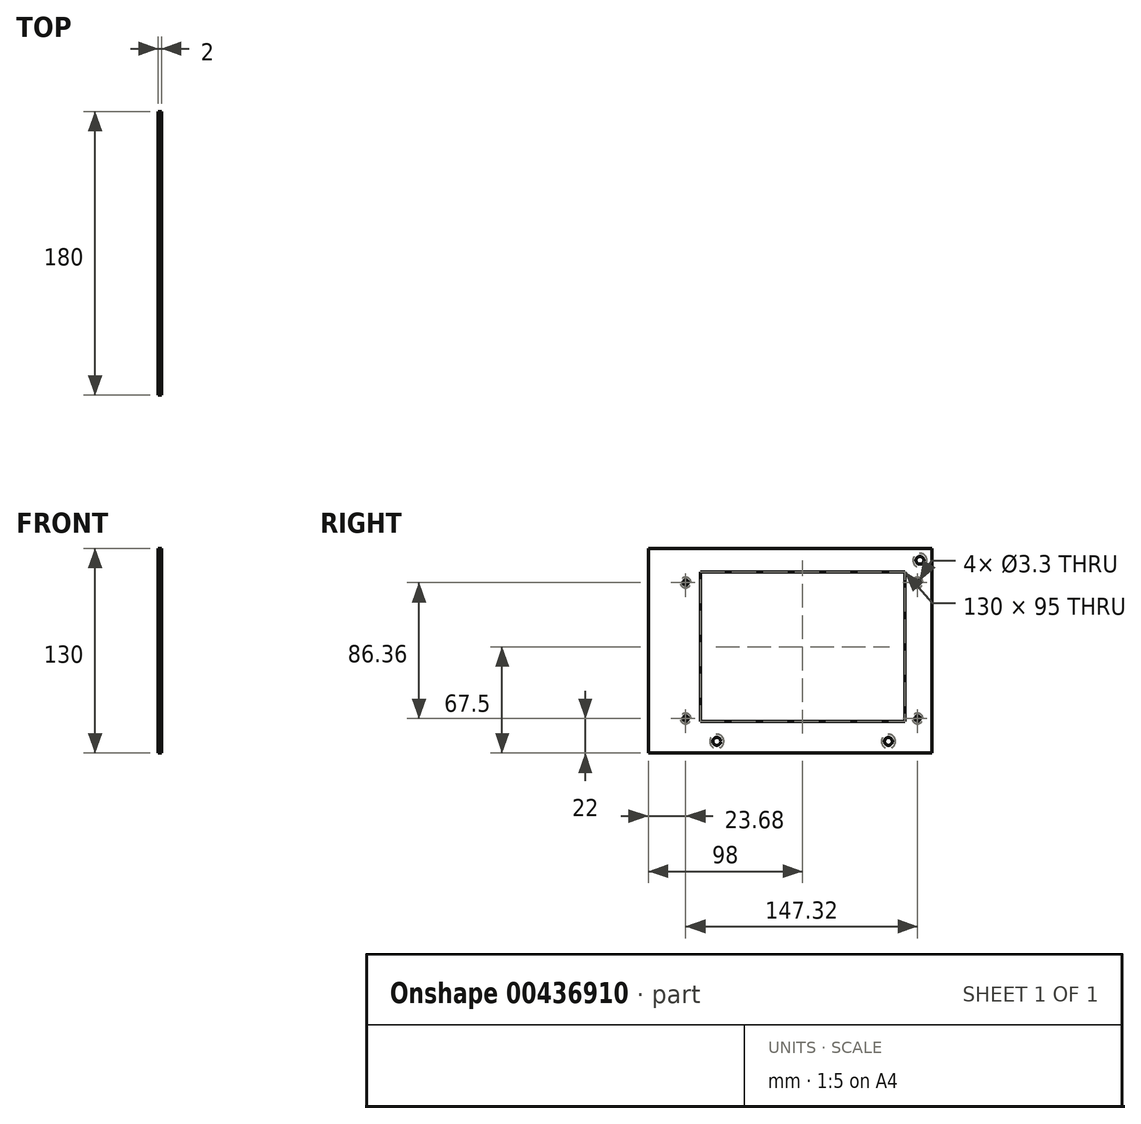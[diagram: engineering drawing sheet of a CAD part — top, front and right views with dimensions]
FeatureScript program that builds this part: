
annotation { "Feature Type Name" : "Feature", "Feature Type Description" : "" }
export const myFeature = defineFeature(function(context is Context, id is Id, definition is map)
    precondition{}
    {
        {
            var Q0;
            Q0=qCreatedBy(makeId("Right.planeOp"),FACE);
            var sketch = newSketch(context, id + "F0", { "sketchPlane" : qUnion([Q0])});
            skLineSegment(sketch, "E0.bottom", {"start": v(0, 0) * mm, "end": v(180, 0) * mm});
            skLineSegment(sketch, "E0.top", {"start": v(0, 130) * mm, "end": v(180, 130) * mm});
            skLineSegment(sketch, "E0.left", {"start": v(0, 0) * mm, "end": v(0, 130) * mm});
            skLineSegment(sketch, "E0.right", {"start": v(180, 0) * mm, "end": v(180, 130) * mm});
            skSolve(sketch);
        }
        {
            var Q0;
            Q0 = qSketchRegion(id + "F0", true);
            extrude(context, id + "F1", {"entities" : qUnion([Q0]), "depth" : 2 * mm});
        }
        {
            var Q0;
            Q0=makeQuery(id+"F1.opExtrude","CAP_FACE",FACE,{"disambiguationData":[OSD([sQuery(id+"F0.wireOp",EDGE,"E0.bottom"),sQuery(id+"F0.wireOp",EDGE,"E0.top"),sQuery(id+"F0.wireOp",EDGE,"E0.left"),sQuery(id+"F0.wireOp",EDGE,"E0.right")])],"isStart":true});
            var sketch = newSketch(context, id + "F2", { "sketchPlane" : qUnion([Q0])});
            skPoint(sketch, "E1", {"position": v(-171, 22) * mm});
            skPoint(sketch, "E2.0.1.0", {"position": v(-171, 108.36) * mm});
            skPoint(sketch, "E2.1.0.0", {"position": v(-23.68, 22) * mm});
            skPoint(sketch, "E2.1.1.0", {"position": v(-23.68, 108.36) * mm});
            skLineSegment(sketch, "E2.direction1", {"start": v(-171, 22) * mm, "end": v(-23.68, 22) * mm, "construction": true});
            skLineSegment(sketch, "E2.direction2", {"start": v(-171, 22) * mm, "end": v(-171, 108.36) * mm, "construction": true});
            skSolve(sketch);
        }
        {
            var Q0;
            Q0=sQuery(id+"F2.wireOp",VERTEX,"E2.0.1.0");
            var Q1;
            Q1=sQuery(id+"F2.wireOp",VERTEX,"E1");
            var Q2;
            Q2=sQuery(id+"F2.wireOp",VERTEX,"E2.1.0.0");
            var Q3;
            Q3=sQuery(id+"F2.wireOp",VERTEX,"E2.1.1.0");
            var Q4;
            Q4=makeQuery(id+"F1.opExtrude","SWEPT_BODY",BODY,{"disambiguationData":[OSD([sQuery(id+"F0.wireOp",EDGE,"E0.bottom"),sQuery(id+"F0.wireOp",EDGE,"E0.top"),sQuery(id+"F0.wireOp",EDGE,"E0.left"),sQuery(id+"F0.wireOp",EDGE,"E0.right")])]});
            hole(context, id + "F3", {"style" : HoleStyle.C_SINK, "endStyle" : HoleEndStyle.THROUGH, "standardTappedOrClearance" : lookupTablePath({ "standard" : "ISO", "fit" : "Normal", "size" : "M3", "type" : "Clearance" }), "standardBlindInLast" : lookupTablePath({ "fit" : "Standard", "standard" : "ISO", "size" : "M3", "type" : "Clearance" }), "holeDiameter" : 3.3 * mm, "cSinkDiameter" : 6.72 * mm, "cSinkAngle" : 90 * degree, "isTappedThrough" : true, "tappedDepth" : 12 * mm, "tapClearance" : 3, "locations" : qUnion([Q0, Q1, Q2, Q3]), "scope" : qUnion([Q4])});
        }
        {
            var Q0;
            Q0=makeQuery(id+"F1.opExtrude","CAP_FACE",FACE,{"disambiguationData":[OSD([sQuery(id+"F0.wireOp",EDGE,"E0.bottom"),sQuery(id+"F0.wireOp",EDGE,"E0.top"),sQuery(id+"F0.wireOp",EDGE,"E0.left"),sQuery(id+"F0.wireOp",EDGE,"E0.right")])],"isStart":true});
            var sketch = newSketch(context, id + "F4", { "sketchPlane" : qUnion([Q0])});
            skLineSegment(sketch, "E3.bottom", {"start": v(-163, 20) * mm, "end": v(-33, 20) * mm});
            skLineSegment(sketch, "E3.top", {"start": v(-163, 115) * mm, "end": v(-33, 115) * mm});
            skLineSegment(sketch, "E3.left", {"start": v(-163, 20) * mm, "end": v(-163, 115) * mm});
            skLineSegment(sketch, "E3.right", {"start": v(-33, 20) * mm, "end": v(-33, 115) * mm});
            skSolve(sketch);
        }
        {
            var Q0;
            Q0 = qSketchRegion(id + "F4", true);
            extrude(context, id + "F5", {"entities" : qUnion([Q0]), "operationType" : NewBodyOperationType.REMOVE, "endBound" : BoundingType.THROUGH_ALL, "oppositeDirection" : true, "depth" : 25 * mm});
        }
        {
            var Q0;
            Q0=makeQuery(id+"F1.opExtrude","CAP_FACE",FACE,{"disambiguationData":[OSD([sQuery(id+"F0.wireOp",EDGE,"E0.bottom"),sQuery(id+"F0.wireOp",EDGE,"E0.top"),sQuery(id+"F0.wireOp",EDGE,"E0.left"),sQuery(id+"F0.wireOp",EDGE,"E0.right")])],"isStart":true});
            var sketch = newSketch(context, id + "F6", { "sketchPlane" : qUnion([Q0])});
            skPoint(sketch, "E4", {"position": v(-152.5, 7.5) * mm});
            skPoint(sketch, "E5", {"position": v(-43.5, 7.5) * mm});
            skPoint(sketch, "E6", {"position": v(-172.5, 122.5) * mm});
            skSolve(sketch);
        }
        {
            var Q0;
            Q0=sQuery(id+"F6.wireOp",VERTEX,"E4");
            var Q1;
            Q1=sQuery(id+"F6.wireOp",VERTEX,"E5");
            var Q2;
            Q2=sQuery(id+"F6.wireOp",VERTEX,"E6");
            var Q3;
            Q3=makeQuery(id+"F1.opExtrude","SWEPT_BODY",BODY,{"disambiguationData":[OSD([sQuery(id+"F0.wireOp",EDGE,"E0.bottom"),sQuery(id+"F0.wireOp",EDGE,"E0.top"),sQuery(id+"F0.wireOp",EDGE,"E0.left"),sQuery(id+"F0.wireOp",EDGE,"E0.right")])]});
            hole(context, id + "F7", {"style" : HoleStyle.C_SINK, "endStyle" : HoleEndStyle.THROUGH, "standardTappedOrClearance" : lookupTablePath({ "standard" : "ISO", "fit" : "Normal", "size" : "M4", "type" : "Clearance" }), "standardBlindInLast" : lookupTablePath({ "fit" : "Standard", "standard" : "ISO", "size" : "M4", "type" : "Clearance" }), "holeDiameter" : 4.4 * mm, "cSinkDiameter" : 8.96 * mm, "cSinkAngle" : 90 * degree, "isTappedThrough" : true, "tappedDepth" : 12 * mm, "tapClearance" : 3, "locations" : qUnion([Q0, Q1, Q2]), "scope" : qUnion([Q3])});
        }
    });
